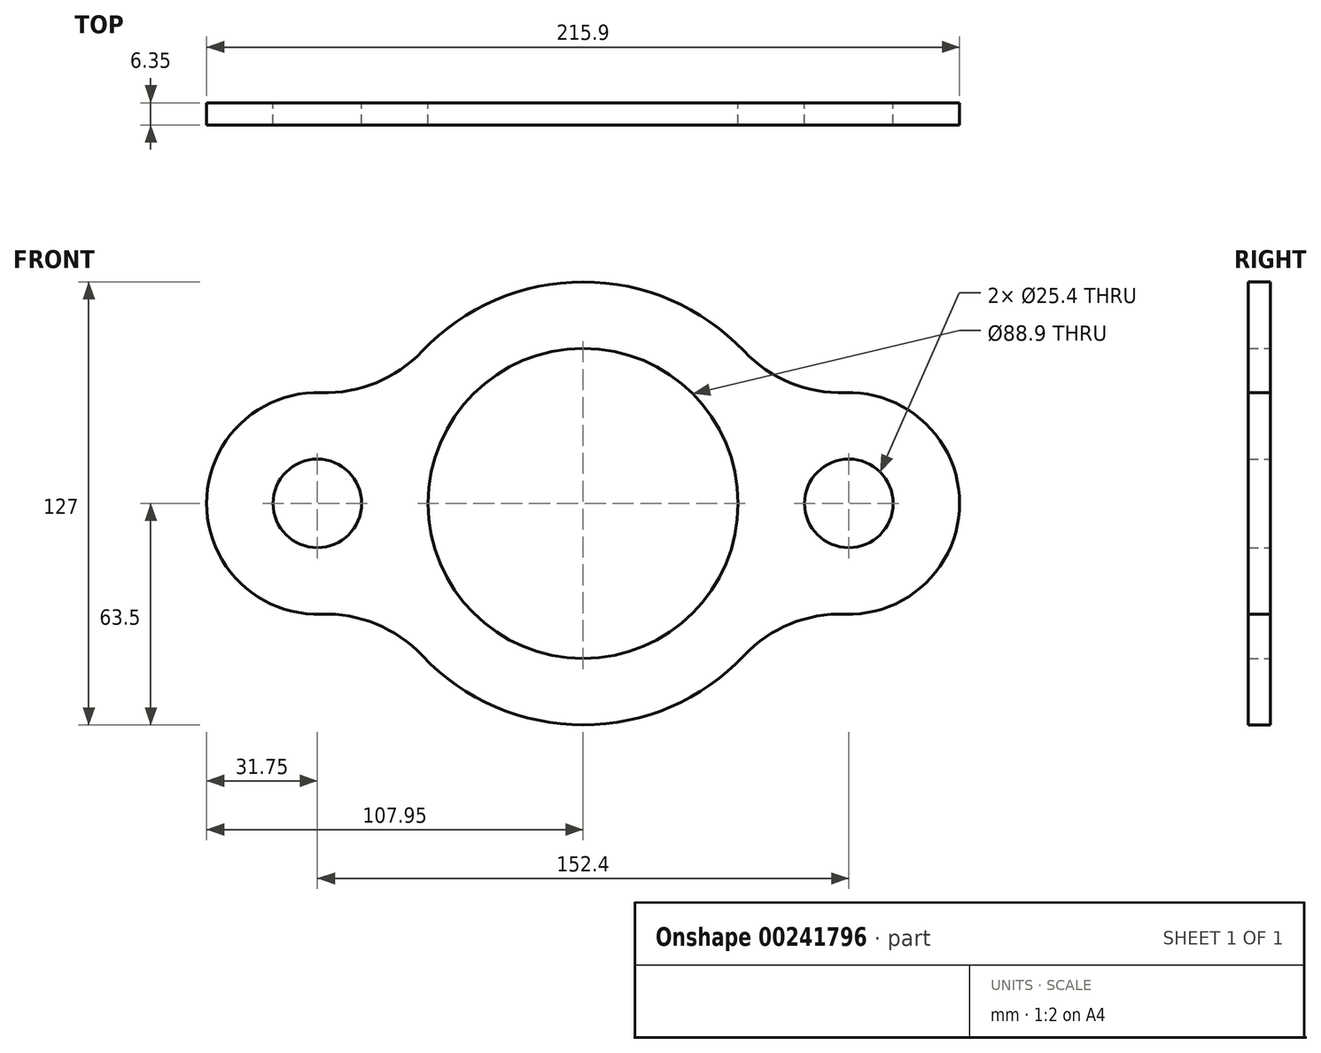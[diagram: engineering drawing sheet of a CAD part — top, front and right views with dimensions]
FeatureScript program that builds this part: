
annotation { "Feature Type Name" : "Feature", "Feature Type Description" : "" }
export const myFeature = defineFeature(function(context is Context, id is Id, definition is map)
    precondition{}
    {
        {
            var Q0;
            Q0=qCreatedBy(makeId("Front.planeOp"),FACE);
            var sketch = newSketch(context, id + "F0", { "sketchPlane" : qUnion([Q0])});
            skCircle(sketch, "E0", {"center": v(0, 0) * mm, "radius": 44.45 * mm});
            skCircle(sketch, "E1", {"center": v(76.2, 0) * mm, "radius": 12.7 * mm});
            skCircle(sketch, "E2", {"center": v(-76.2, 0) * mm, "radius": 12.7 * mm});
            skArc(sketch, "E3", {"start": v(-75.12, 31.73) * mm, "mid": v(-107.95, 0) * mm, "end": v(-75.12, -31.73) * mm});
            skArc(sketch, "E4", {"start": v(75.12, -31.73) * mm, "mid": v(107.95, 0) * mm, "end": v(75.12, 31.73) * mm});
            skArc(sketch, "E5", {"start": v(-46.14, -43.63) * mm, "mid": v(0, -63.5) * mm, "end": v(46.14, -43.63) * mm});
            skArc(sketch, "E6", {"start": v(-75.12, 31.73) * mm, "mid": v(-59.35, 34.56) * mm, "end": v(-46.14, 43.63) * mm});
            skArc(sketch, "E7.trimOffspring", {"start": v(46.14, 43.63) * mm, "mid": v(0, 63.5) * mm, "end": v(-46.14, 43.63) * mm});
            skPoint(sketch, "E8.visualSharp", {"position": v(57.94, 25.98) * mm});
            skArc(sketch, "E8.filletArc", {"start": v(46.14, 43.63) * mm, "mid": v(59.35, 34.56) * mm, "end": v(75.12, 31.73) * mm});
            skPoint(sketch, "E9.visualSharp", {"position": v(57.94, -25.98) * mm});
            skArc(sketch, "E9.filletArc", {"start": v(75.12, -31.73) * mm, "mid": v(59.35, -34.56) * mm, "end": v(46.14, -43.63) * mm});
            skPoint(sketch, "E10.visualSharp", {"position": v(-57.94, -25.98) * mm});
            skArc(sketch, "E10.filletArc", {"start": v(-46.14, -43.63) * mm, "mid": v(-59.35, -34.56) * mm, "end": v(-75.12, -31.73) * mm});
            skSolve(sketch);
        }
        {
            var Q0;
            Q0 = qSketchRegion(id + "F0", true);
            extrude(context, id + "F1", {"entities" : qUnion([Q0]), "depth" : 6.35 * mm});
        }
    });
